# Revit family: DAL_A3-Garage-Timber-Side-Hung-(1)
name_source: partatom
category: Doors
revit_build: Autodesk Revit 2016 (Build: 20150220_1215(x64)
units: mm (PartAtom-declared; Revit-internal decimal feet)

## family parameters
Always vertical = Yes
Cut with Voids When Loaded = No
Host = Wall
Room Calculation Point = No
Shared = No

## types (2) — shared parameters
Cavity Closer Offset from Ext = 102.5 mm  [stored 0.336286 ft]
Cavity Closer Width = 50 mm  [stored 0.164042 ft]
Door Panel Thickness = 32 mm  [stored 0.104987 ft]
FrameDepth = 89 mm  [stored 0.291995 ft]
FrameOffset - External = 25 mm  [stored 0.082021 ft]
FrameWidth = 42 mm  [stored 0.137795 ft]
Function = Interior
Glazing Panel Height = 450 mm  [stored 1.47638 ft]
Handle Z Distance = 1050 mm
Keynote = L20
Manufacturer = Revit
Material Door = Door - Panel
Material Frame = Door -  Frame/Mullion
O/A Frame Width = 64 mm  [stored 0.209974 ft]
Operation = DoubleDoorSingleSwing
Rough Width = 2271 mm  [stored 7.45079 ft]
Stile Lock Rail = 200 mm  [stored 0.656168 ft]
Structural Tolerance = 8 mm  [stored 0.0262467 ft]
Thickness = 32 mm  [stored 0.104987 ft]
Tolerance = 3 mm  [stored 0.00984252 ft]
Undercut = 10 mm  [stored 0.0328084 ft]
Vis - Cavity Closers = Yes
Wall Closure = By host
Width = 2271 mm  [stored 7.45079 ft]
Wrap Layers (Ext) from Ext = 102.5 mm  [stored 0.336286 ft]
Wrap Layers (Int) from Ext = 177.5 mm

## per-type parameters (varying)
| type | Cavity Closer Depth | Height | Rough Height | Stile Bottom Rail | Stile Hanging | Stile Shutting | Stile Top Rail |
| 2271 x 2052mm | 75 mm | 2052 mm  [stored 6.73228 ft] | 2052 mm  [stored 6.73228 ft] | 250 mm  [stored 0.82021 ft] | 175 mm  [stored 0.574147 ft] | 100 mm  [stored 0.328084 ft] | 200 mm  [stored 0.656168 ft] |
| 2271 x 2205mm Garage Door | 85 mm  [stored 0.278871 ft] | 2205 mm  [stored 7.23425 ft] | 2205 mm  [stored 7.23425 ft] | 25 mm  [stored 0.082021 ft] | 75 mm | 75 mm | 100 mm  [stored 0.328084 ft] |

note: [stored X ft] marks values corroborated as IEEE doubles in the binary element streams (Revit-internal decimal feet)

## geometry (parser evidence)
native form markers: Sweep x2
no freeform markers — native parametric forms only
